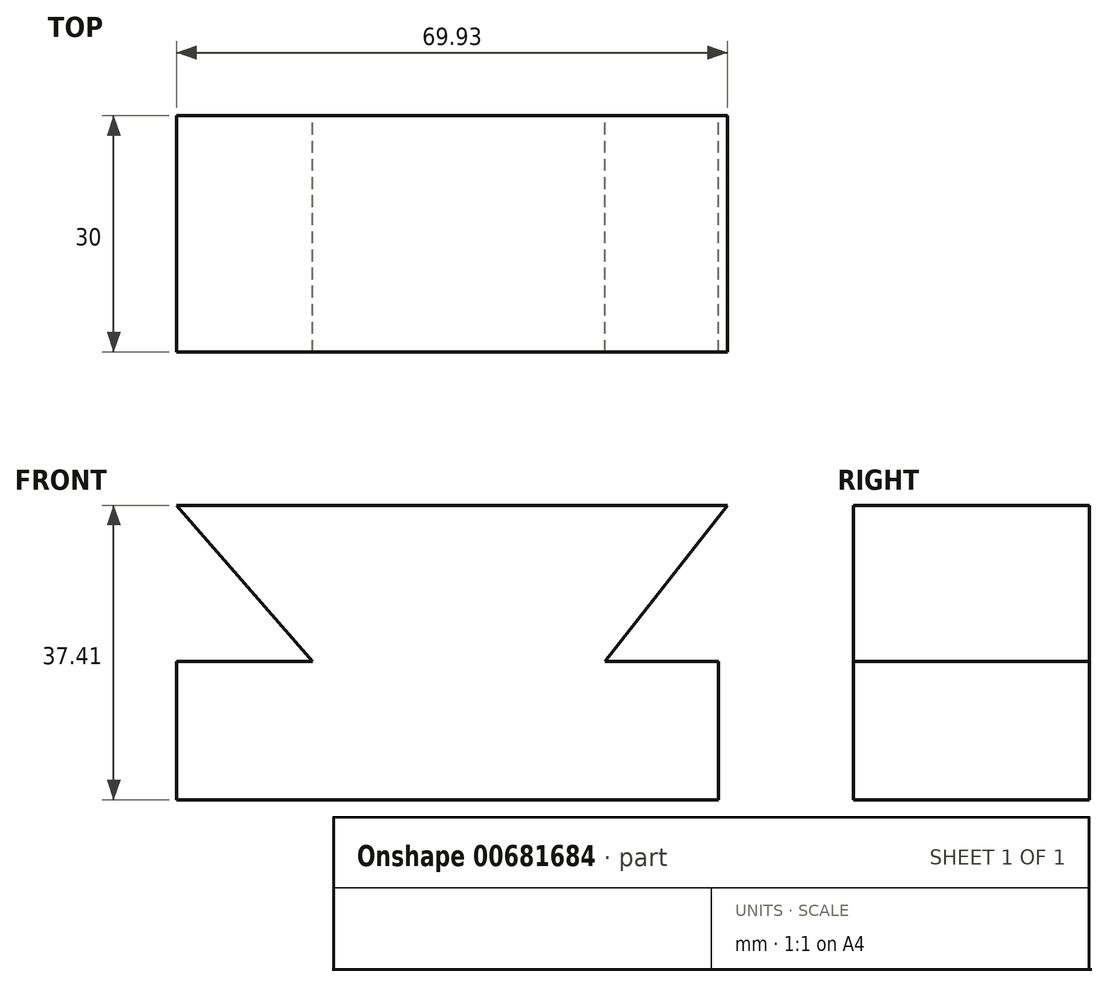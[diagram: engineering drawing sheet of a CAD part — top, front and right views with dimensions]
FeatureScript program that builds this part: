
annotation { "Feature Type Name" : "Feature", "Feature Type Description" : "" }
export const myFeature = defineFeature(function(context is Context, id is Id, definition is map)
    precondition{}
    {
        {
            var Q0;
            Q0=qCreatedBy(makeId("Front.planeOp"),FACE);
            var sketch = newSketch(context, id + "F0", { "sketchPlane" : qUnion([Q0])});
            skLineSegment(sketch, "E0", {"start": v(-36.98, 30.36) * mm, "end": v(32.95, 30.36) * mm});
            skLineSegment(sketch, "E1", {"start": v(-36.98, 30.36) * mm, "end": v(-19.71, 10.5) * mm});
            skLineSegment(sketch, "E2", {"start": v(-19.71, 10.5) * mm, "end": v(-36.98, 10.5) * mm});
            skLineSegment(sketch, "E3", {"start": v(-36.98, 10.5) * mm, "end": v(-36.98, -7.05) * mm});
            skLineSegment(sketch, "E4", {"start": v(-36.98, -7.05) * mm, "end": v(31.8, -7.05) * mm});
            skLineSegment(sketch, "E5", {"start": v(31.8, -7.05) * mm, "end": v(31.8, 10.5) * mm});
            skLineSegment(sketch, "E6", {"start": v(31.8, 10.5) * mm, "end": v(17.41, 10.5) * mm});
            skLineSegment(sketch, "E7", {"start": v(17.41, 10.5) * mm, "end": v(32.95, 30.36) * mm});
            skSolve(sketch);
        }
        {
            var Q0;
            Q0 = qSketchRegion(id + "F0", true);
            extrude(context, id + "F1", {"entities" : qUnion([Q0]), "depth" : 30 * mm, "offsetDistance" : 25 * mm});
        }
    });
